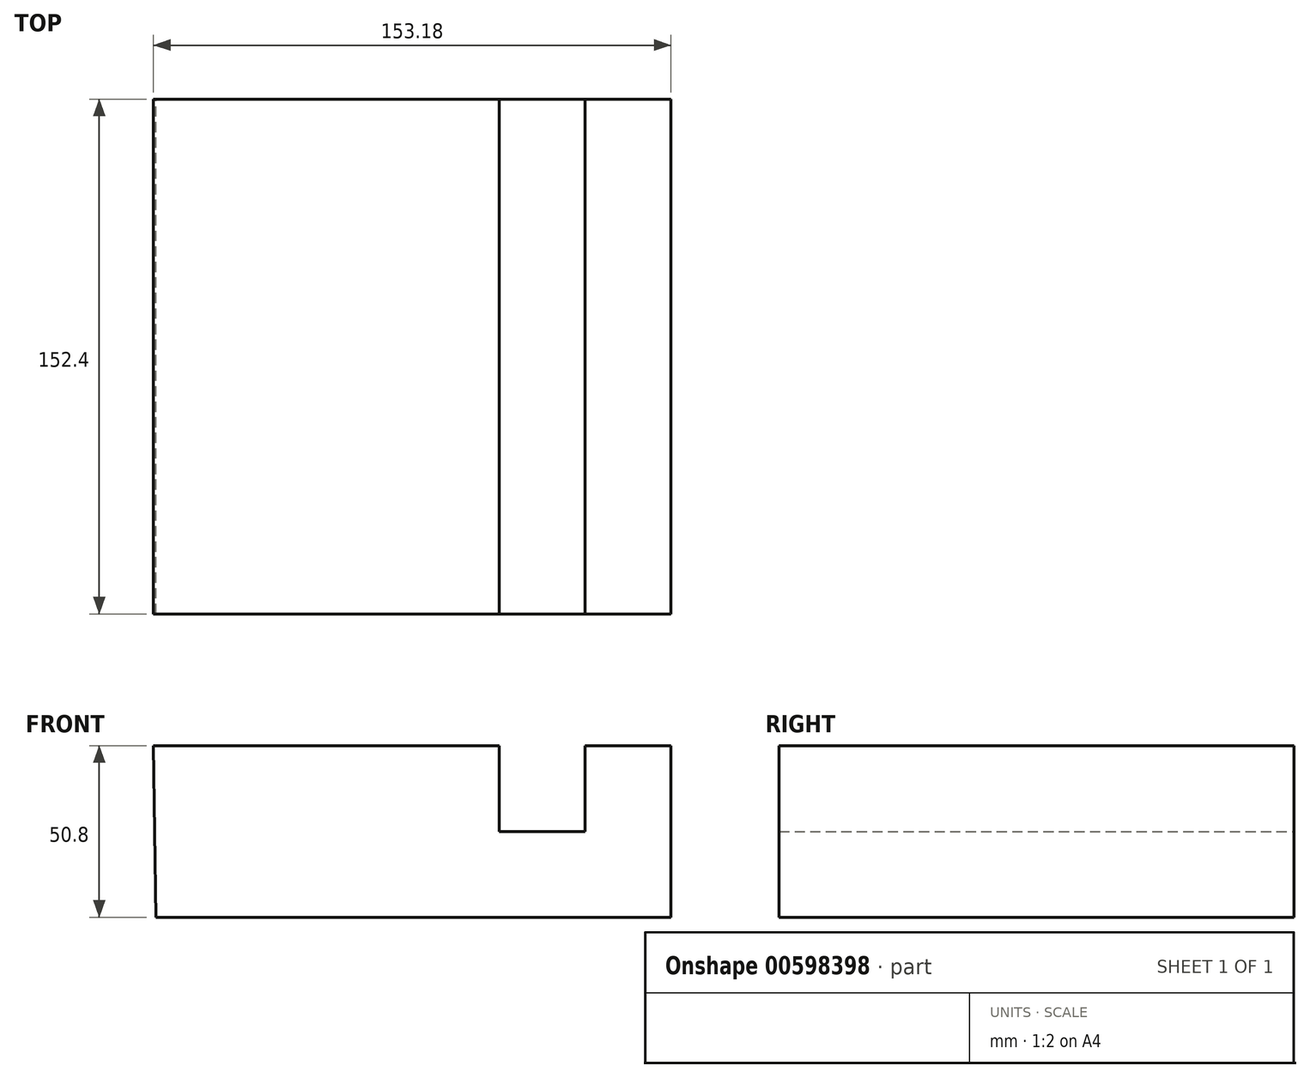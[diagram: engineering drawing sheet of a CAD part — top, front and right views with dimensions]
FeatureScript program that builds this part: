
annotation { "Feature Type Name" : "Feature", "Feature Type Description" : "" }
export const myFeature = defineFeature(function(context is Context, id is Id, definition is map)
    precondition{}
    {
        {
            var Q0;
            Q0=qCreatedBy(makeId("Front.planeOp"),FACE);
            var sketch = newSketch(context, id + "F0", { "sketchPlane" : qUnion([Q0])});
            skLineSegment(sketch, "E0", {"start": v(-76.21, 0) * mm, "end": v(76.19, 0) * mm});
            skLineSegment(sketch, "E1", {"start": v(76.19, 0) * mm, "end": v(76.19, 50.8) * mm});
            skLineSegment(sketch, "E2", {"start": v(76.19, 50.8) * mm, "end": v(50.79, 50.8) * mm});
            skLineSegment(sketch, "E3", {"start": v(50.79, 50.8) * mm, "end": v(50.79, 25.4) * mm});
            skLineSegment(sketch, "E4", {"start": v(50.79, 25.4) * mm, "end": v(25.39, 25.4) * mm});
            skLineSegment(sketch, "E5", {"start": v(25.39, 25.4) * mm, "end": v(25.39, 50.8) * mm});
            skLineSegment(sketch, "E6", {"start": v(25.39, 50.8) * mm, "end": v(-77, 50.8) * mm});
            skLineSegment(sketch, "E7", {"start": v(-77, 50.8) * mm, "end": v(-76.21, 0) * mm});
            skSolve(sketch);
        }
        {
            var Q0;
            Q0 = qSketchRegion(id + "F0", true);
            extrude(context, id + "F1", {"entities" : qUnion([Q0]), "depth" : 152.4 * mm, "offsetDistance" : 25.4 * mm});
        }
    });
